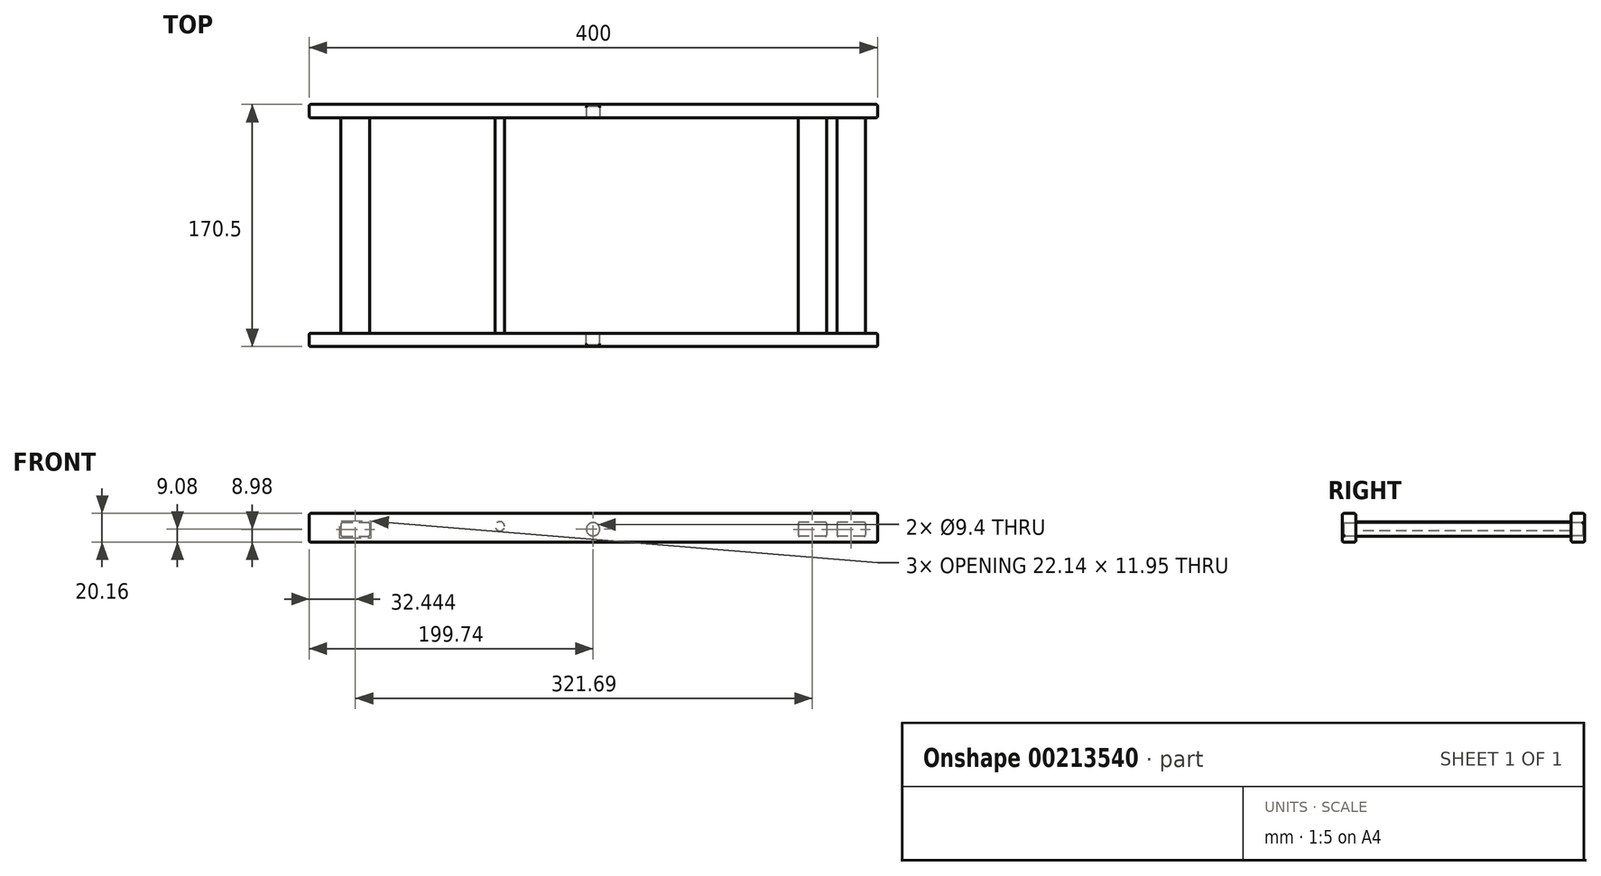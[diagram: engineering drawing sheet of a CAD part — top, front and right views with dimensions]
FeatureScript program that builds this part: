
annotation { "Feature Type Name" : "Feature", "Feature Type Description" : "" }
export const myFeature = defineFeature(function(context is Context, id is Id, definition is map)
    precondition{}
    {
        {
            var Q0;
            Q0=qCreatedBy(makeId("Front.planeOp"),FACE);
            var sketch = newSketch(context, id + "F0", { "sketchPlane" : qUnion([Q0])});
            skLineSegment(sketch, "E0.bottom", {"start": v(200, -10.07) * mm, "end": v(-200, -10.08) * mm});
            skLineSegment(sketch, "E0.top", {"start": v(200, 10.08) * mm, "end": v(-200, 10.07) * mm});
            skLineSegment(sketch, "E0.left", {"start": v(200, -10.07) * mm, "end": v(200, 10.08) * mm});
            skLineSegment(sketch, "E0.right", {"start": v(-200, -10.08) * mm, "end": v(-200, 10.07) * mm});
            skPoint(sketch, "E0.middle", {"position": v(0, 0) * mm});
            skSolve(sketch);
        }
        {
            var Q0;
            Q0=makeQuery(id+"F0.imprint","IMPRINT",FACE,{"disambiguationData":[TD([[makeQuery(id+"F0.imprint","IMPRINT",EDGE,{"derivedFrom":sQuery(id+"F0.wireOp",EDGE,"E0.bottom")}),-1.0]])]});
            extrude(context, id + "F1", {"entities" : qUnion([Q0]), "depth" : 9.4 * mm});
        }
        {
            var Q0;
            Q0=makeQuery(id+"F1.opExtrude","CAP_FACE",FACE,{"disambiguationData":[OSD([sQuery(id+"F0.wireOp",EDGE,"E0.bottom"),sQuery(id+"F0.wireOp",EDGE,"E0.top"),sQuery(id+"F0.wireOp",EDGE,"E0.left"),sQuery(id+"F0.wireOp",EDGE,"E0.right")])],"isStart":false});
            var sketch = newSketch(context, id + "F2", { "sketchPlane" : qUnion([Q0])});
            skLineSegment(sketch, "E1.bottom", {"start": v(-177.62, 3.87) * mm, "end": v(-157.49, 3.87) * mm});
            skLineSegment(sketch, "E1.top", {"start": v(-177.62, -6.08) * mm, "end": v(-157.49, -6.08) * mm});
            skLineSegment(sketch, "E1.left", {"start": v(-177.62, 3.87) * mm, "end": v(-177.62, -6.08) * mm});
            skLineSegment(sketch, "E1.right", {"start": v(-157.49, 3.87) * mm, "end": v(-157.49, -6.07) * mm});
            skLineSegment(sketch, "E2.bottom", {"start": v(191.5, 3.88) * mm, "end": v(171.36, 3.88) * mm});
            skLineSegment(sketch, "E2.top", {"start": v(191.5, -6.07) * mm, "end": v(171.36, -6.07) * mm});
            skLineSegment(sketch, "E2.left", {"start": v(191.5, 3.88) * mm, "end": v(191.5, -6.07) * mm});
            skLineSegment(sketch, "E2.right", {"start": v(171.36, 3.88) * mm, "end": v(171.36, -6.07) * mm});
            skLineSegment(sketch, "E3.bottom", {"start": v(164.2, 3.88) * mm, "end": v(144.06, 3.88) * mm});
            skLineSegment(sketch, "E3.top", {"start": v(164.2, -6.07) * mm, "end": v(144.06, -6.07) * mm});
            skLineSegment(sketch, "E3.left", {"start": v(164.2, 3.88) * mm, "end": v(164.2, -6.07) * mm});
            skLineSegment(sketch, "E3.right", {"start": v(144.06, 3.88) * mm, "end": v(144.06, -6.07) * mm});
            skSolve(sketch);
        }
        {
            var Q0;
            Q0=makeQuery(id+"F2.imprint","IMPRINT",FACE,{"disambiguationData":[TD([[makeQuery(id+"F2.imprint","IMPRINT",EDGE,{"derivedFrom":sQuery(id+"F2.wireOp",EDGE,"E1.bottom")}),-1.0]])]});
            var Q1;
            Q1=makeQuery(id+"F2.imprint","IMPRINT",FACE,{"disambiguationData":[TD([[makeQuery(id+"F2.imprint","IMPRINT",EDGE,{"derivedFrom":sQuery(id+"F2.wireOp",EDGE,"E3.bottom")}),1.0]])]});
            var Q2;
            Q2=makeQuery(id+"F2.imprint","IMPRINT",FACE,{"disambiguationData":[TD([[makeQuery(id+"F2.imprint","IMPRINT",EDGE,{"derivedFrom":sQuery(id+"F2.wireOp",EDGE,"E2.bottom")}),1.0]])]});
            extrude(context, id + "F3", {"entities" : qUnion([Q0, Q1, Q2]), "operationType" : NewBodyOperationType.ADD, "depth" : 151.7 * mm});
        }
        {
            var Q0;
            Q0=makeQuery(id+"F3.opExtrude","CAP_FACE",FACE,{"disambiguationData":[OSD([sQuery(id+"F2.wireOp",EDGE,"E1.bottom"),sQuery(id+"F2.wireOp",EDGE,"E1.top"),sQuery(id+"F2.wireOp",EDGE,"E1.left"),sQuery(id+"F2.wireOp",EDGE,"E1.right")])],"isStart":false});
            var sketch = newSketch(context, id + "F4", { "sketchPlane" : qUnion([Q0])});
            skLineSegment(sketch, "E4.bottom", {"start": v(200, -10.07) * mm, "end": v(-200, -10.08) * mm});
            skLineSegment(sketch, "E4.top", {"start": v(200, 10.08) * mm, "end": v(-200, 10.08) * mm});
            skLineSegment(sketch, "E4.left", {"start": v(200, -10.07) * mm, "end": v(200, 10.08) * mm});
            skLineSegment(sketch, "E4.right", {"start": v(-200, -10.08) * mm, "end": v(-200, 10.08) * mm});
            skPoint(sketch, "E4.middle", {"position": v(0, 0) * mm});
            skSolve(sketch);
        }
        {
            var Q0;
            Q0 = qSketchRegion(id + "F4", true);
            extrude(context, id + "F5", {"entities" : qUnion([Q0]), "operationType" : NewBodyOperationType.ADD, "depth" : 9.4 * mm});
        }
        {
            var Q0;
            Q0=makeQuery(id+"F5.opExtrude","CAP_FACE",FACE,{"disambiguationData":[OSD([sQuery(id+"F4.wireOp",EDGE,"E4.bottom"),sQuery(id+"F4.wireOp",EDGE,"E4.top"),sQuery(id+"F4.wireOp",EDGE,"E4.left"),sQuery(id+"F4.wireOp",EDGE,"E4.right")])],"isStart":true});
            var sketch = newSketch(context, id + "F6", { "sketchPlane" : qUnion([Q0])});
            skCircle(sketch, "E5", {"center": v(0.26, -1) * mm, "radius": 4.7 * mm});
            skLineSegment(sketch, "E6", {"start": v(200, 0) * mm, "end": v(-200, 0) * mm, "construction": true});
            skSolve(sketch);
        }
        {
            var Q0;
            Q0=makeQuery(id+"F6.imprint","IMPRINT",FACE,{"disambiguationData":[TD([[makeQuery(id+"F6.imprint","IMPRINT",EDGE,{"derivedFrom":sQuery(id+"F6.wireOp",EDGE,"E5")}),1.0]])]});
            extrude(context, id + "F7", {"entities" : qUnion([Q0]), "operationType" : NewBodyOperationType.REMOVE, "oppositeDirection" : true, "depth" : 8.4 * mm});
        }
        {
            var Q0;
            Q0=makeQuery(id+"F1.opExtrude","CAP_FACE",FACE,{"disambiguationData":[OSD([sQuery(id+"F0.wireOp",EDGE,"E0.bottom"),sQuery(id+"F0.wireOp",EDGE,"E0.top"),sQuery(id+"F0.wireOp",EDGE,"E0.left"),sQuery(id+"F0.wireOp",EDGE,"E0.right")])],"isStart":false});
            var sketch = newSketch(context, id + "F8", { "sketchPlane" : qUnion([Q0])});
            skLineSegment(sketch, "E7", {"start": v(-200, 0) * mm, "end": v(200, 0) * mm, "construction": true});
            skCircle(sketch, "E8", {"center": v(-0.26, -1) * mm, "radius": 4.7 * mm});
            skSolve(sketch);
        }
        {
            var Q0;
            Q0=makeQuery(id+"F8.imprint","IMPRINT",FACE,{"disambiguationData":[TD([[makeQuery(id+"F8.imprint","IMPRINT",EDGE,{"derivedFrom":sQuery(id+"F8.wireOp",EDGE,"E8")}),1.0]])]});
            extrude(context, id + "F9", {"entities" : qUnion([Q0]), "operationType" : NewBodyOperationType.REMOVE, "oppositeDirection" : true, "depth" : 8.4 * mm});
        }
        {
            var Q0;
            Q0=makeQuery(id+"F5.opExtrude","CAP_FACE",FACE,{"disambiguationData":[OSD([sQuery(id+"F4.wireOp",EDGE,"E4.bottom"),sQuery(id+"F4.wireOp",EDGE,"E4.top"),sQuery(id+"F4.wireOp",EDGE,"E4.left"),sQuery(id+"F4.wireOp",EDGE,"E4.right")])],"isStart":true});
            var sketch = newSketch(context, id + "F10", { "sketchPlane" : qUnion([Q0])});
            skCircle(sketch, "E9", {"center": v(65.84, 1.08) * mm, "radius": 3.25 * mm});
            skSolve(sketch);
        }
        {
            var Q0;
            Q0=makeQuery(id+"F10.imprint","IMPRINT",FACE,{"disambiguationData":[TD([[makeQuery(id+"F10.imprint","IMPRINT",EDGE,{"derivedFrom":sQuery(id+"F10.wireOp",EDGE,"E9")}),1.0]])]});
            var Q1;
            Q1=makeQuery(id+"F1.opExtrude","CAP_FACE",FACE,{"disambiguationData":[OSD([sQuery(id+"F0.wireOp",EDGE,"E0.bottom"),sQuery(id+"F0.wireOp",EDGE,"E0.top"),sQuery(id+"F0.wireOp",EDGE,"E0.left"),sQuery(id+"F0.wireOp",EDGE,"E0.right")])],"isStart":false});
            extrude(context, id + "F11", {"entities" : qUnion([Q0]), "operationType" : NewBodyOperationType.ADD, "endBound" : BoundingType.UP_TO_SURFACE, "endBoundEntityFace" : qUnion([Q1]), "depth" : 25 * mm});
        }
        {
            var Q0;
            Q0=makeQuery(id+"F5.opExtrude","CAP_FACE",FACE,{"disambiguationData":[OSD([sQuery(id+"F4.wireOp",EDGE,"E4.bottom"),sQuery(id+"F4.wireOp",EDGE,"E4.top"),sQuery(id+"F4.wireOp",EDGE,"E4.left"),sQuery(id+"F4.wireOp",EDGE,"E4.right")])],"isStart":false});
            var Q1;
            Q1=makeQuery(id+"F3.opExtrude","SWEPT_FACE",FACE,{"disambiguationData":[OSD([sQuery(id+"F2.wireOp",EDGE,"E2.bottom")])]});
            var Q2;
            Q2=makeQuery(id+"F3.opExtrude","SWEPT_FACE",FACE,{"disambiguationData":[OSD([sQuery(id+"F2.wireOp",EDGE,"E3.bottom")])]});
            var Q3;
            Q3=makeQuery(id+"F1.opExtrude","CAP_FACE",FACE,{"disambiguationData":[OSD([sQuery(id+"F0.wireOp",EDGE,"E0.bottom"),sQuery(id+"F0.wireOp",EDGE,"E0.top"),sQuery(id+"F0.wireOp",EDGE,"E0.left"),sQuery(id+"F0.wireOp",EDGE,"E0.right")])],"isStart":false});
            var Q4;
            Q4=makeQuery(id+"F5.opExtrude","SWEPT_FACE",FACE,{"disambiguationData":[OSD([sQuery(id+"F4.wireOp",EDGE,"E4.left")])]});
            var Q5;
            Q5=makeQuery(id+"F5.opExtrude","CAP_EDGE",EDGE,{"disambiguationData":[OSD([sQuery(id+"F4.wireOp",EDGE,"E4.top")])],"isStart":true});
            var Q6;
            Q6=makeQuery(id+"F1.opExtrude","SWEPT_FACE",FACE,{"disambiguationData":[OSD([sQuery(id+"F0.wireOp",EDGE,"E0.top")])]});
            var Q7;
            Q7=makeQuery(id+"F1.opExtrude","SWEPT_FACE",FACE,{"disambiguationData":[OSD([sQuery(id+"F0.wireOp",EDGE,"E0.left")])]});
            var Q8;
            Q8=makeQuery(id+"F3.opExtrude","SWEPT_FACE",FACE,{"disambiguationData":[OSD([sQuery(id+"F2.wireOp",EDGE,"E1.right")])]});
            var Q9;
            Q9=makeQuery(id+"F3.opExtrude","SWEPT_FACE",FACE,{"disambiguationData":[OSD([sQuery(id+"F2.wireOp",EDGE,"E1.bottom")])]});
            var Q10;
            Q10=makeQuery(id+"F5.opExtrude","SWEPT_FACE",FACE,{"disambiguationData":[OSD([sQuery(id+"F4.wireOp",EDGE,"E4.right")])]});
            var Q11;
            Q11=makeQuery(id+"F5.opExtrude","SWEPT_FACE",FACE,{"disambiguationData":[OSD([sQuery(id+"F4.wireOp",EDGE,"E4.bottom")])]});
            var Q12;
            Q12=makeQuery(id+"F3.opExtrude","SWEPT_FACE",FACE,{"disambiguationData":[OSD([sQuery(id+"F2.wireOp",EDGE,"E1.left")])]});
            var Q13;
            Q13=makeQuery(id+"F3.opExtrude","SWEPT_FACE",FACE,{"disambiguationData":[OSD([sQuery(id+"F2.wireOp",EDGE,"E1.top")])]});
            var Q14;
            Q14=makeQuery(id+"F5.opExtrude","CAP_FACE",FACE,{"disambiguationData":[OSD([sQuery(id+"F4.wireOp",EDGE,"E4.bottom"),sQuery(id+"F4.wireOp",EDGE,"E4.top"),sQuery(id+"F4.wireOp",EDGE,"E4.left"),sQuery(id+"F4.wireOp",EDGE,"E4.right")])],"isStart":true});
            var Q15;
            Q15=makeQuery(id+"F1.opExtrude","SWEPT_FACE",FACE,{"disambiguationData":[OSD([sQuery(id+"F0.wireOp",EDGE,"E0.right")])]});
            var Q16;
            Q16=makeQuery(id+"F1.opExtrude","CAP_FACE",FACE,{"disambiguationData":[OSD([sQuery(id+"F0.wireOp",EDGE,"E0.bottom"),sQuery(id+"F0.wireOp",EDGE,"E0.top"),sQuery(id+"F0.wireOp",EDGE,"E0.left"),sQuery(id+"F0.wireOp",EDGE,"E0.right")])],"isStart":true});
            var Q17;
            Q17=makeQuery(id+"F3.opExtrude","SWEPT_FACE",FACE,{"disambiguationData":[OSD([sQuery(id+"F2.wireOp",EDGE,"E2.top")])]});
            var Q18;
            Q18=makeQuery(id+"F3.opExtrude","SWEPT_FACE",FACE,{"disambiguationData":[OSD([sQuery(id+"F2.wireOp",EDGE,"E3.top")])]});
            var Q19;
            Q19=makeQuery(id+"F3.opExtrude","SWEPT_FACE",FACE,{"disambiguationData":[OSD([sQuery(id+"F2.wireOp",EDGE,"E3.left")])]});
            var Q20;
            Q20=makeQuery(id+"F7.boolean.opBoolean","COPY",FACE,{"derivedFrom":makeQuery(id+"F7.opExtrude","CAP_FACE",FACE,{"disambiguationData":[OSD([sQuery(id+"F6.wireOp",EDGE,"E5")])],"isStart":false})});
            var Q21;
            Q21=makeQuery(id+"F9.boolean.opBoolean","COPY",EDGE,{"derivedFrom":makeQuery(id+"F9.opExtrude","CAP_EDGE",EDGE,{"disambiguationData":[OSD([sQuery(id+"F8.wireOp",EDGE,"E8")])],"isStart":false})});
            fillet(context, id + "F12", {"entities" : qUnion([Q0, Q1, Q2, Q3, Q4, Q5, Q6, Q7, Q8, Q9, Q10, Q11, Q12, Q13, Q14, Q15, Q16, Q17, Q18, Q19, Q20, Q21]), "radius" : 1 * mm, "tangentPropagation" : true, "allowEdgeOverflow" : false});
        }
    });
